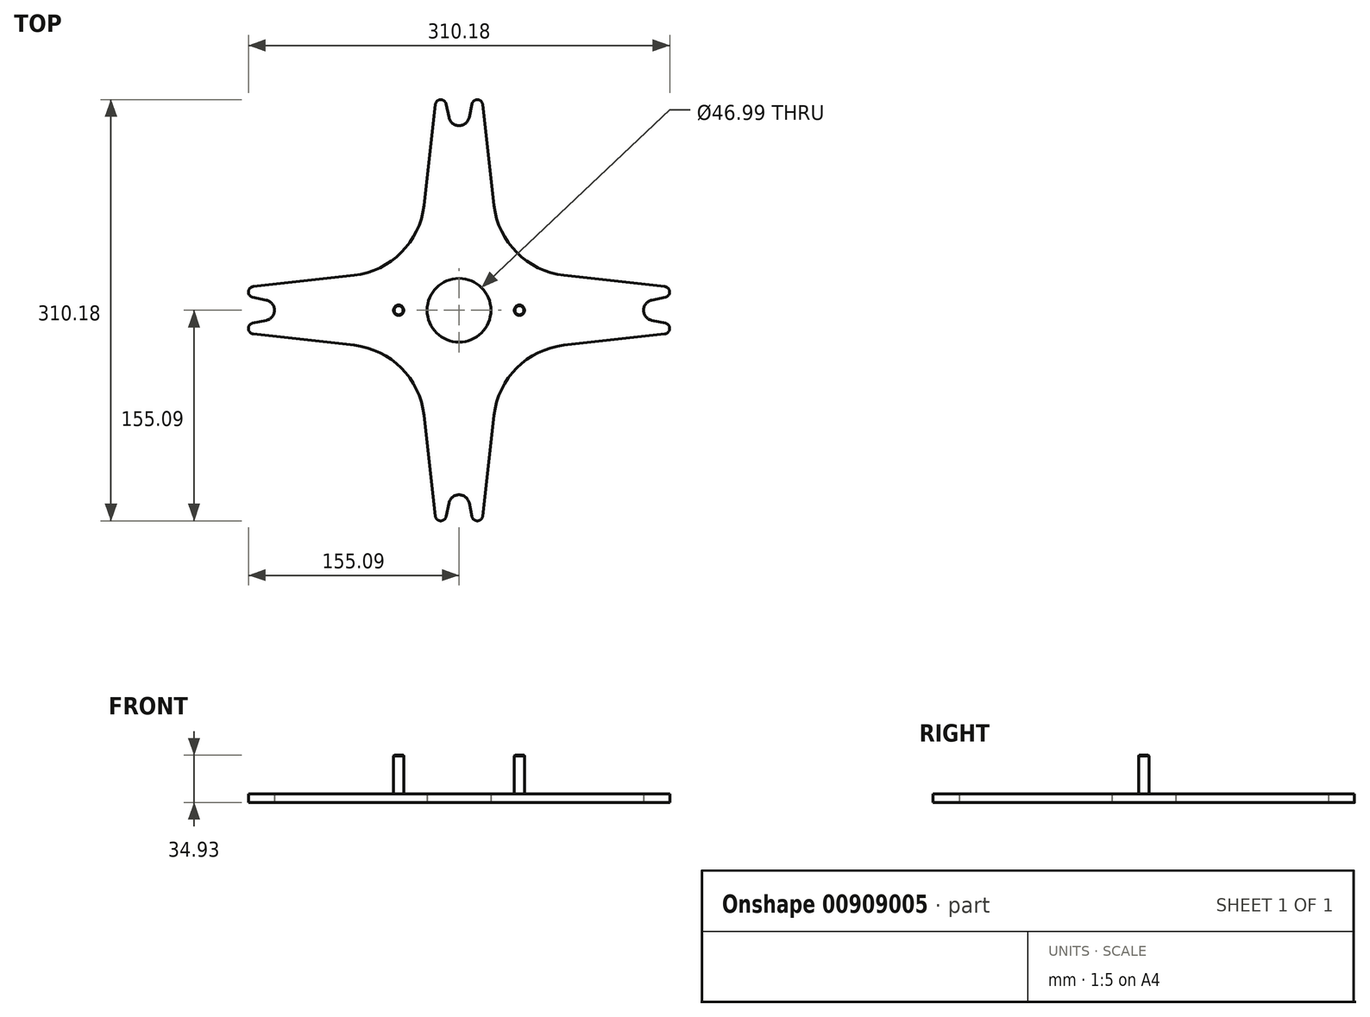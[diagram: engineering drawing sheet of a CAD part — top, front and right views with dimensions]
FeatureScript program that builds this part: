
annotation { "Feature Type Name" : "Feature", "Feature Type Description" : "" }
export const myFeature = defineFeature(function(context is Context, id is Id, definition is map)
    precondition{}
    {
        {
            var Q0;
            Q0=qCreatedBy(makeId("Top.planeOp"),FACE);
            var sketch = newSketch(context, id + "F0", { "sketchPlane" : qUnion([Q0])});
            skCircle(sketch, "E0", {"center": v(0, 0) * mm, "radius": 23.5 * mm});
            skArc(sketch, "E1", {"start": v(-141.92, -7.45) * mm, "mid": v(-135.9, 0) * mm, "end": v(-141.92, 7.45) * mm});
            skArc(sketch, "E2", {"start": v(-151.57, 17.4) * mm, "mid": v(-155.09, 13.65) * mm, "end": v(-151.95, 9.59) * mm});
            skArc(sketch, "E3", {"start": v(-151.95, -9.59) * mm, "mid": v(-155.09, -13.65) * mm, "end": v(-151.57, -17.4) * mm});
            skLineSegment(sketch, "E4", {"start": v(-151.95, 9.59) * mm, "end": v(-141.92, 7.45) * mm});
            skLineSegment(sketch, "E5", {"start": v(-151.95, -9.59) * mm, "end": v(-141.92, -7.45) * mm});
            skArc(sketch, "E6", {"start": v(-77.28, 25.77) * mm, "mid": v(-42.51, 42.51) * mm, "end": v(-25.77, 77.28) * mm});
            skLineSegment(sketch, "E7", {"start": v(-151.57, 17.4) * mm, "end": v(-77.28, 25.77) * mm});
            skArc(sketch, "E8", {"start": v(-25.77, -77.28) * mm, "mid": v(-42.51, -42.51) * mm, "end": v(-77.28, -25.77) * mm});
            skLineSegment(sketch, "E9", {"start": v(-151.57, -17.4) * mm, "end": v(-77.28, -25.77) * mm});
            skArc(sketch, "E10.1.0", {"start": v(7.45, -141.92) * mm, "mid": v(0, -135.9) * mm, "end": v(-7.45, -141.92) * mm});
            skArc(sketch, "E10.1.1", {"start": v(83.82, -25.4) * mm, "mid": v(44.9, -40.26) * mm, "end": v(25.77, -77.28) * mm});
            skLineSegment(sketch, "E10.1.3", {"start": v(-17.4, -151.57) * mm, "end": v(-25.77, -77.28) * mm});
            skLineSegment(sketch, "E10.1.4", {"start": v(17.4, -151.57) * mm, "end": v(25.77, -77.28) * mm});
            skArc(sketch, "E10.1.5", {"start": v(-17.4, -151.57) * mm, "mid": v(-13.65, -155.09) * mm, "end": v(-9.59, -151.95) * mm});
            skLineSegment(sketch, "E10.1.6", {"start": v(9.59, -151.95) * mm, "end": v(7.45, -141.92) * mm});
            skLineSegment(sketch, "E10.1.7", {"start": v(-9.59, -151.95) * mm, "end": v(-7.45, -141.92) * mm});
            skArc(sketch, "E10.1.8", {"start": v(9.59, -151.95) * mm, "mid": v(13.65, -155.09) * mm, "end": v(17.4, -151.57) * mm});
            skArc(sketch, "E10.2.0", {"start": v(141.92, 7.45) * mm, "mid": v(135.9, 0) * mm, "end": v(141.92, -7.45) * mm});
            skArc(sketch, "E10.2.1", {"start": v(25.77, 77.28) * mm, "mid": v(42.51, 42.51) * mm, "end": v(77.28, 25.77) * mm});
            skArc(sketch, "E10.2.2", {"start": v(83.82, -25.4) * mm, "mid": v(44.9, -40.26) * mm, "end": v(25.77, -77.28) * mm});
            skLineSegment(sketch, "E10.2.3", {"start": v(151.57, -17.4) * mm, "end": v(77.28, -25.77) * mm});
            skLineSegment(sketch, "E10.2.4", {"start": v(151.57, 17.4) * mm, "end": v(77.28, 25.77) * mm});
            skArc(sketch, "E10.2.5", {"start": v(151.57, -17.4) * mm, "mid": v(155.09, -13.65) * mm, "end": v(151.95, -9.59) * mm});
            skLineSegment(sketch, "E10.2.6", {"start": v(151.95, 9.59) * mm, "end": v(141.92, 7.45) * mm});
            skLineSegment(sketch, "E10.2.7", {"start": v(151.95, -9.59) * mm, "end": v(141.92, -7.45) * mm});
            skArc(sketch, "E10.2.8", {"start": v(151.95, 9.59) * mm, "mid": v(155.09, 13.65) * mm, "end": v(151.57, 17.4) * mm});
            skArc(sketch, "E10.3.0", {"start": v(-7.45, 141.92) * mm, "mid": v(0, 135.9) * mm, "end": v(7.45, 141.92) * mm});
            skArc(sketch, "E10.3.2", {"start": v(25.77, 77.28) * mm, "mid": v(42.51, 42.51) * mm, "end": v(77.28, 25.77) * mm});
            skLineSegment(sketch, "E10.3.3", {"start": v(17.4, 151.57) * mm, "end": v(25.77, 77.28) * mm});
            skLineSegment(sketch, "E10.3.4", {"start": v(-17.4, 151.57) * mm, "end": v(-25.77, 77.28) * mm});
            skArc(sketch, "E10.3.5", {"start": v(17.4, 151.57) * mm, "mid": v(13.65, 155.09) * mm, "end": v(9.59, 151.95) * mm});
            skLineSegment(sketch, "E10.3.6", {"start": v(-9.59, 151.95) * mm, "end": v(-7.45, 141.92) * mm});
            skLineSegment(sketch, "E10.3.7", {"start": v(9.59, 151.95) * mm, "end": v(7.45, 141.92) * mm});
            skArc(sketch, "E10.3.8", {"start": v(-9.59, 151.95) * mm, "mid": v(-13.65, 155.09) * mm, "end": v(-17.4, 151.57) * mm});
            skSolve(sketch);
        }
        {
            var Q0;
            Q0=makeQuery(id+"F0.imprint","IMPRINT",FACE,{"disambiguationData":[TD([[makeQuery(id+"F0.imprint","IMPRINT",EDGE,{"derivedFrom":sQuery(id+"F0.wireOp",EDGE,"E0")}),-1.0]])]});
            extrude(context, id + "F1", {"entities" : qUnion([Q0]), "depth" : 6.35 * mm, "offsetDistance" : 25.4 * mm});
        }
        {
            var Q0;
            Q0=makeQuery(id+"F1.opExtrude","CAP_FACE",FACE,{"disambiguationData":[OSD([sQuery(id+"F0.wireOp",EDGE,"E0"),sQuery(id+"F0.wireOp",EDGE,"E1"),sQuery(id+"F0.wireOp",EDGE,"E2"),sQuery(id+"F0.wireOp",EDGE,"E3"),sQuery(id+"F0.wireOp",EDGE,"E4"),sQuery(id+"F0.wireOp",EDGE,"E5"),sQuery(id+"F0.wireOp",EDGE,"E7"),sQuery(id+"F0.wireOp",EDGE,"E9"),sQuery(id+"F0.wireOp",EDGE,"E10.1.0"),sQuery(id+"F0.wireOp",EDGE,"E8"),sQuery(id+"F0.wireOp",EDGE,"E10.1.3"),sQuery(id+"F0.wireOp",EDGE,"E10.1.4"),sQuery(id+"F0.wireOp",EDGE,"E10.1.5"),sQuery(id+"F0.wireOp",EDGE,"E10.1.6"),sQuery(id+"F0.wireOp",EDGE,"E10.1.7"),sQuery(id+"F0.wireOp",EDGE,"E10.1.8"),sQuery(id+"F0.wireOp",EDGE,"E10.2.0"),sQuery(id+"F0.wireOp",EDGE,"E10.2.2"),sQuery(id+"F0.wireOp",EDGE,"E10.2.3"),sQuery(id+"F0.wireOp",EDGE,"E10.2.4"),sQuery(id+"F0.wireOp",EDGE,"E10.2.5"),sQuery(id+"F0.wireOp",EDGE,"E10.2.6"),sQuery(id+"F0.wireOp",EDGE,"E10.2.7"),sQuery(id+"F0.wireOp",EDGE,"E10.2.8"),sQuery(id+"F0.wireOp",EDGE,"E10.3.0"),sQuery(id+"F0.wireOp",EDGE,"E6"),sQuery(id+"F0.wireOp",EDGE,"E10.3.2"),sQuery(id+"F0.wireOp",EDGE,"E10.3.3"),sQuery(id+"F0.wireOp",EDGE,"E10.3.4"),sQuery(id+"F0.wireOp",EDGE,"E10.3.5"),sQuery(id+"F0.wireOp",EDGE,"E10.3.6"),sQuery(id+"F0.wireOp",EDGE,"E10.3.7"),sQuery(id+"F0.wireOp",EDGE,"E10.3.8")])],"isStart":false});
            var sketch = newSketch(context, id + "F2", { "sketchPlane" : qUnion([Q0])});
            skCircle(sketch, "E11", {"center": v(-44.45, 0) * mm, "radius": 3.81 * mm});
            skCircle(sketch, "E12", {"center": v(44.45, 0) * mm, "radius": 3.81 * mm});
            skSolve(sketch);
        }
        {
            var Q0;
            Q0=makeQuery(id+"F2.imprint","IMPRINT",FACE,{"disambiguationData":[TD([[makeQuery(id+"F2.imprint","IMPRINT",EDGE,{"derivedFrom":sQuery(id+"F2.wireOp",EDGE,"E11")}),1.0]])]});
            var Q1;
            Q1=makeQuery(id+"F2.imprint","IMPRINT",FACE,{"disambiguationData":[TD([[makeQuery(id+"F2.imprint","IMPRINT",EDGE,{"derivedFrom":sQuery(id+"F2.wireOp",EDGE,"E12")}),1.0]])]});
            extrude(context, id + "F3", {"entities" : qUnion([Q0, Q1]), "operationType" : NewBodyOperationType.ADD, "depth" : 28.57 * mm, "offsetDistance" : 25.4 * mm});
        }
        {
            var Q0;
            Q0=makeQuery(id+"F3.opExtrude","CAP_EDGE",EDGE,{"disambiguationData":[OSD([sQuery(id+"F2.wireOp",EDGE,"E11")])],"isStart":false});
            var Q1;
            Q1=makeQuery(id+"F3.opExtrude","CAP_EDGE",EDGE,{"disambiguationData":[OSD([sQuery(id+"F2.wireOp",EDGE,"E12")])],"isStart":false});
            chamfer(context, id + "F4", {"entities" : qUnion([Q0, Q1]), "width" : 0.5 * mm, "tangentPropagation" : true});
        }
    });
